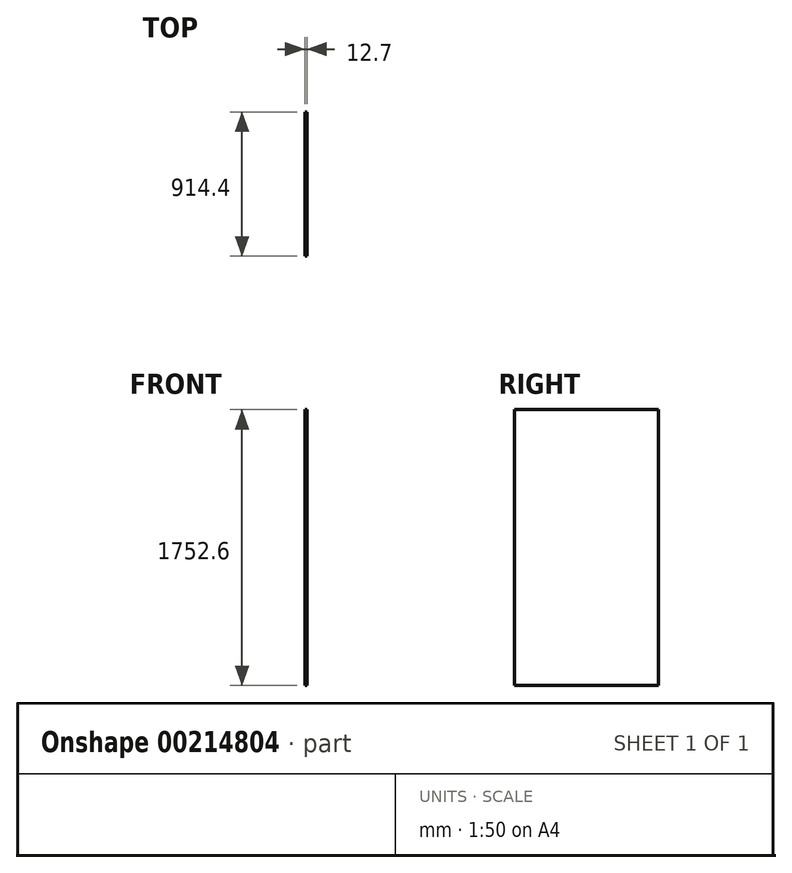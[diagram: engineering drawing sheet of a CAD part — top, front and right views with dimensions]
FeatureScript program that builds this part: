
annotation { "Feature Type Name" : "Feature", "Feature Type Description" : "" }
export const myFeature = defineFeature(function(context is Context, id is Id, definition is map)
    precondition{}
    {
        {
            var Q0;
            Q0=qCreatedBy(makeId("Right.planeOp"),FACE);
            var sketch = newSketch(context, id + "F0", { "sketchPlane" : qUnion([Q0])});
            skLineSegment(sketch, "E0.bottom", {"start": v(0, 0) * mm, "end": v(914.4, 0) * mm});
            skLineSegment(sketch, "E0.top", {"start": v(0, -1752.6) * mm, "end": v(914.4, -1752.6) * mm});
            skLineSegment(sketch, "E0.left", {"start": v(0, 0) * mm, "end": v(0, -1752.6) * mm});
            skLineSegment(sketch, "E0.right", {"start": v(914.4, 0) * mm, "end": v(914.4, -1752.6) * mm});
            skSolve(sketch);
        }
        {
            var Q0;
            Q0=makeQuery(id+"F0.imprint","IMPRINT",FACE,{"disambiguationData":[TD([[makeQuery(id+"F0.imprint","IMPRINT",EDGE,{"derivedFrom":sQuery(id+"F0.wireOp",EDGE,"E0.bottom")}),-1.0]])]});
            extrude(context, id + "F1", {"entities" : qUnion([Q0]), "depth" : 12.7 * mm});
        }
    });
